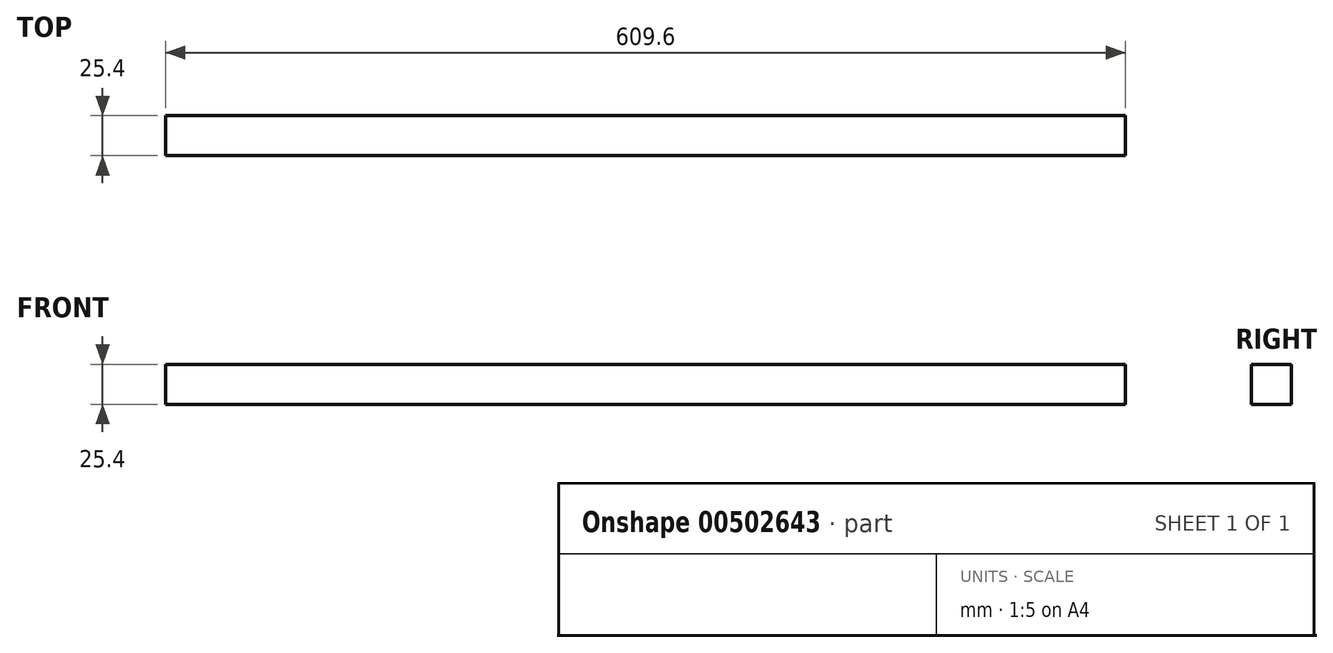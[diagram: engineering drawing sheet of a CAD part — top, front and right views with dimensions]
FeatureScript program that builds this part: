
annotation { "Feature Type Name" : "Feature", "Feature Type Description" : "" }
export const myFeature = defineFeature(function(context is Context, id is Id, definition is map)
    precondition{}
    {
        {
            var Q0;
            Q0=qCreatedBy(makeId("Front.planeOp"),FACE);
            var sketch = newSketch(context, id + "F0", { "sketchPlane" : qUnion([Q0])});
            skLineSegment(sketch, "E0.bottom", {"start": v(-245.98, 25.4) * mm, "end": v(363.62, 25.4) * mm});
            skLineSegment(sketch, "E0.top", {"start": v(-245.98, 0) * mm, "end": v(363.62, 0) * mm});
            skLineSegment(sketch, "E0.left", {"start": v(-245.98, 25.4) * mm, "end": v(-245.98, 0) * mm});
            skLineSegment(sketch, "E0.right", {"start": v(363.62, 25.4) * mm, "end": v(363.62, 0) * mm});
            skSolve(sketch);
        }
        {
            var Q0;
            Q0=makeQuery(id+"F0.imprint","IMPRINT",FACE,{"disambiguationData":[TD([[makeQuery(id+"F0.imprint","IMPRINT",EDGE,{"derivedFrom":sQuery(id+"F0.wireOp",EDGE,"E0.bottom")}),-1.0]])]});
            extrude(context, id + "F1", {"entities" : qUnion([Q0]), "depth" : 25.4 * mm});
        }
    });
